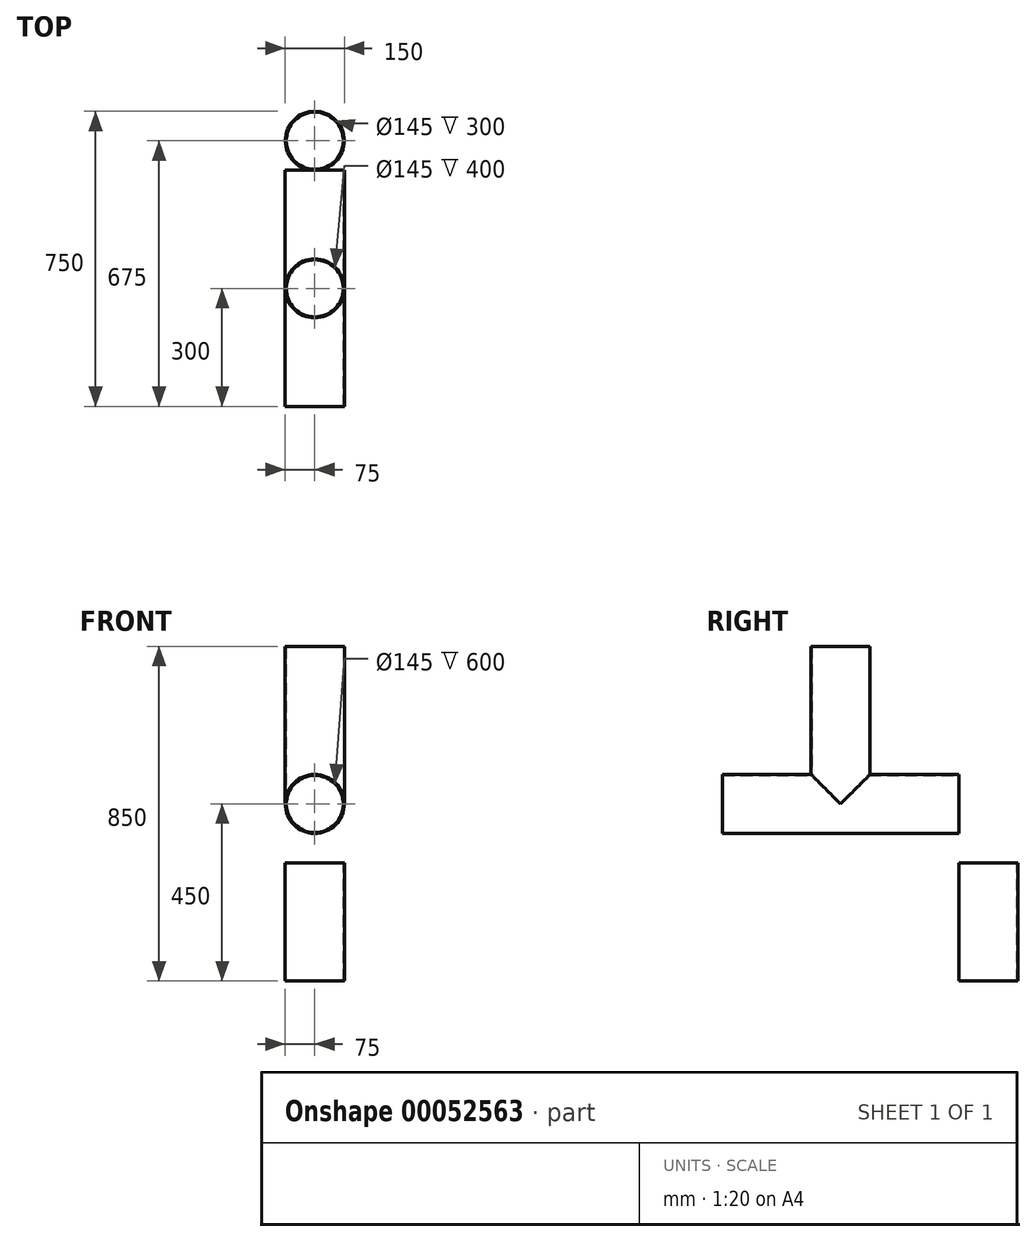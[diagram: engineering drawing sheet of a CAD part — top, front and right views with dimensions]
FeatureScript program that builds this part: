
annotation { "Feature Type Name" : "Feature", "Feature Type Description" : "" }
export const myFeature = defineFeature(function(context is Context, id is Id, definition is map)
    precondition{}
    {
        {
            var Q0;
            Q0=qCreatedBy(makeId("Top.planeOp"),FACE);
            var sketch = newSketch(context, id + "F0", { "sketchPlane" : qUnion([Q0])});
            skCircle(sketch, "E0", {"center": v(0, 0) * mm, "radius": 75 * mm});
            skSolve(sketch);
        }
        {
            var Q0;
            Q0=makeQuery(id+"F0.imprint","IMPRINT",FACE,{"disambiguationData":[TD([[makeQuery(id+"F0.imprint","IMPRINT",EDGE,{"derivedFrom":sQuery(id+"F0.wireOp",EDGE,"E0")}),1.0]])]});
            extrude(context, id + "F1", {"entities" : qUnion([Q0]), "depth" : 400 * mm});
        }
        {
            var Q0;
            Q0=qCreatedBy(makeId("Front.planeOp"),FACE);
            var sketch = newSketch(context, id + "F2", { "sketchPlane" : qUnion([Q0])});
            skCircle(sketch, "E1", {"center": v(0, 0) * mm, "radius": 75 * mm});
            skSolve(sketch);
        }
        {
            var Q0;
            Q0=makeQuery(id+"F2.imprint","IMPRINT",FACE,{"disambiguationData":[TD([[makeQuery(id+"F2.imprint","IMPRINT",EDGE,{"derivedFrom":sQuery(id+"F2.wireOp",EDGE,"E1")}),1.0]])]});
            extrude(context, id + "F3", {"entities" : qUnion([Q0]), "operationType" : NewBodyOperationType.ADD, "endBound" : BoundingType.SYMMETRIC, "depth" : 600 * mm});
        }
        {
            var Q0;
            Q0=makeQuery(id+"F3.opExtrude","CAP_FACE",FACE,{"disambiguationData":[OSD([sQuery(id+"F2.wireOp",EDGE,"E1")])],"isStart":false});
            shell(context, id + "F4", {"entities" : qUnion([Q0]), "thickness" : 2.5 * mm});
        }
        {
            var Q0;
            Q0=makeQuery(id+"F1.opExtrude","CAP_FACE",FACE,{"disambiguationData":[OSD([sQuery(id+"F0.wireOp",EDGE,"E0")])],"isStart":false});
            var sketch = newSketch(context, id + "F5", { "sketchPlane" : qUnion([Q0])});
            skCircle(sketch, "E2.0", {"center": v(0, 0) * mm, "radius": 75 * mm});
            skCircle(sketch, "E3.0", {"center": v(0, 0) * mm, "radius": 72.5 * mm});
            skSolve(sketch);
        }
        {
            var Q0;
            Q0=makeQuery(id+"F5.imprint","IMPRINT",FACE,{"disambiguationData":[TD([[makeQuery(id+"F5.imprint","IMPRINT",EDGE,{"derivedFrom":sQuery(id+"F5.wireOp",EDGE,"E3.0")}),1.0]])]});
            extrude(context, id + "F6", {"entities" : qUnion([Q0]), "operationType" : NewBodyOperationType.REMOVE, "oppositeDirection" : true, "depth" : 2.5 * mm});
        }
        {
            var Q0;
            Q0=makeQuery(id+"F3.opExtrude","CAP_FACE",FACE,{"disambiguationData":[OSD([sQuery(id+"F2.wireOp",EDGE,"E1")])],"isStart":true});
            var sketch = newSketch(context, id + "F7", { "sketchPlane" : qUnion([Q0])});
            skCircle(sketch, "E4.0", {"center": v(0, 0) * mm, "radius": 75 * mm});
            skCircle(sketch, "E5.0", {"center": v(0, 0) * mm, "radius": 72.5 * mm});
            skSolve(sketch);
        }
        {
            var Q0;
            Q0=makeQuery(id+"F7.imprint","IMPRINT",FACE,{"disambiguationData":[TD([[makeQuery(id+"F7.imprint","IMPRINT",EDGE,{"derivedFrom":sQuery(id+"F7.wireOp",EDGE,"E5.0")}),1.0]])]});
            extrude(context, id + "F8", {"entities" : qUnion([Q0]), "operationType" : NewBodyOperationType.REMOVE, "oppositeDirection" : true, "depth" : 2.5 * mm});
        }
        {
            var Q0;
            Q0=qCreatedBy(makeId("Top.planeOp"),FACE);
            cPlane(context, id + "F9", {"entities" : qUnion([Q0]), "cplaneType" : CPlaneType.OFFSET, "offset" : 150 * mm, "oppositeDirection" : true, "width" : 150 * mm, "height" : 150 * mm});
        }
        {
            var Q0;
            Q0=qCreatedBy(id+"F9.planeOp",FACE);
            var sketch = newSketch(context, id + "F10", { "sketchPlane" : qUnion([Q0])});
            skPoint(sketch, "E6", {"position": v(0, 375) * mm});
            skCircle(sketch, "E7", {"center": v(0, 375) * mm, "radius": 75 * mm});
            skSolve(sketch);
        }
        {
            var Q0;
            Q0=makeQuery(id+"F10.imprint","IMPRINT",FACE,{"disambiguationData":[TD([[makeQuery(id+"F10.imprint","IMPRINT",EDGE,{"derivedFrom":sQuery(id+"F10.wireOp",EDGE,"E7")}),1.0]])]});
            extrude(context, id + "F11", {"entities" : qUnion([Q0]), "oppositeDirection" : true, "depth" : 300 * mm});
        }
        {
            var Q0;
            Q0=makeQuery(id+"F11.opExtrude","CAP_FACE",FACE,{"disambiguationData":[OSD([sQuery(id+"F10.wireOp",EDGE,"E7")])],"isStart":true});
            var sketch = newSketch(context, id + "F12", { "sketchPlane" : qUnion([Q0])});
            skCircle(sketch, "E8.0.0", {"center": v(0, 375) * mm, "radius": 75 * mm});
            skCircle(sketch, "E9.0", {"center": v(0, 375) * mm, "radius": 72.5 * mm});
            skSolve(sketch);
        }
        {
            var Q0;
            Q0=makeQuery(id+"F12.imprint","IMPRINT",FACE,{"disambiguationData":[TD([[makeQuery(id+"F12.imprint","IMPRINT",EDGE,{"derivedFrom":sQuery(id+"F12.wireOp",EDGE,"E9.0")}),1.0]])]});
            extrude(context, id + "F13", {"entities" : qUnion([Q0]), "operationType" : NewBodyOperationType.REMOVE, "endBound" : BoundingType.THROUGH_ALL, "oppositeDirection" : true, "depth" : 25 * mm});
        }
    });
